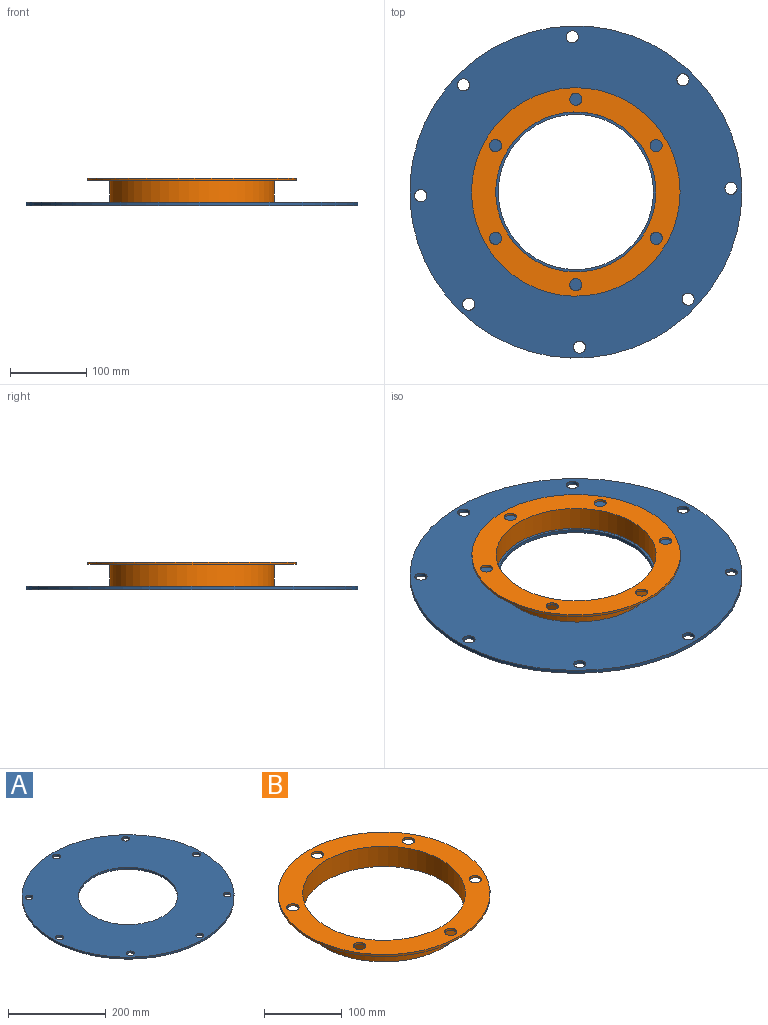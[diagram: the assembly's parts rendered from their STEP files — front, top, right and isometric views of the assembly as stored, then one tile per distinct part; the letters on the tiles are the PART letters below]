
ASSEMBLY  parts=2 mates=1
PART A: 12 faces, bbox 435x435x4.8 mm
  f0: cylinder r=217.49mm len=434.98mm, axis (0,0,-1), area 6508mm2, adj f1,f2
  f1: plane 434.98x434.98mm, normal (0,0,1), area 114587.1mm2, adj f0,f3,f4,f5,f6,f7,f8,f9
  f2: plane 434.98x434.98mm, normal (0,0,-1), area 114587.1mm2, adj f0,f3,f4,f5,f6,f7,f8,f9
  f3: cylinder r=7.94mm len=15.88mm, axis (0,0,1), area 237.5mm2, adj f1,f2
  f4: cylinder r=7.94mm len=15.88mm, axis (0,0,1), area 237.5mm2, adj f1,f2
  f5: cylinder r=7.94mm len=15.88mm, axis (0,0,1), area 237.5mm2, adj f1,f2
  f6: cylinder r=7.94mm len=15.88mm, axis (0,0,1), area 237.5mm2, adj f1,f2
  f7: cylinder r=7.94mm len=15.88mm, axis (0,0,1), area 237.5mm2, adj f1,f2
  f8: cylinder r=7.94mm len=15.88mm, axis (0,0,1), area 237.5mm2, adj f1,f2
  f9: cylinder r=7.94mm len=15.88mm, axis (0,0,1), area 237.5mm2, adj f1,f2
  f10: cylinder r=7.94mm len=15.88mm, axis (0,0,1), area 237.5mm2, adj f1,f2
  f11: cylinder r=101.6mm len=203.2mm, axis (0,0,1), area 3040.2mm2, adj f1,f2
PART B: 12 faces, bbox 273.1x273.1x31.8 mm
  f0: plane 273.05x273.05mm, normal (0,0,1), area 22881mm2, adj f1,f5,f6,f7,f8,f9,f10,f11
  f1: cylinder r=104.77mm len=209.55mm, axis (0,0,1), area 20901.7mm2, adj f0,f2
  f2: plane 215.9x215.9mm, normal (0,0,-1), area 2121.8mm2, adj f1,f3
  f3: cylinder r=107.95mm len=215.9mm, axis (0,0,1), area 19381.6mm2, adj f2,f4
  f4: plane 273.05x273.05mm, normal (0,0,-1), area 20759.2mm2, adj f3,f5,f6,f7,f8,f9,f10,f11
  f5: cylinder r=136.53mm len=273.05mm, axis (0,0,1), area 2723.6mm2, adj f0,f4
  f6: cylinder r=7.94mm len=15.88mm, axis (0,0,1), area 158.3mm2, adj f0,f4
  f7: cylinder r=7.94mm len=15.88mm, axis (0,0,1), area 158.3mm2, adj f0,f4
  f8: cylinder r=7.94mm len=15.88mm, axis (0,0,1), area 158.3mm2, adj f0,f4
  f9: cylinder r=7.94mm len=15.88mm, axis (0,0,1), area 158.3mm2, adj f0,f4
  f10: cylinder r=7.94mm len=15.88mm, axis (0,0,1), area 158.3mm2, adj f0,f4
  f11: cylinder r=7.94mm len=15.88mm, axis (0,0,1), area 158.3mm2, adj f0,f4
PLACE A t=(-485.67,-237.12,14.65)mm
PLACE B t=(-63.96,19.1,51.16)mm
MATE fastened A.f0 <-> B.f1  axis (0,0,1) through (-63.96,19.1,19.41)mm
